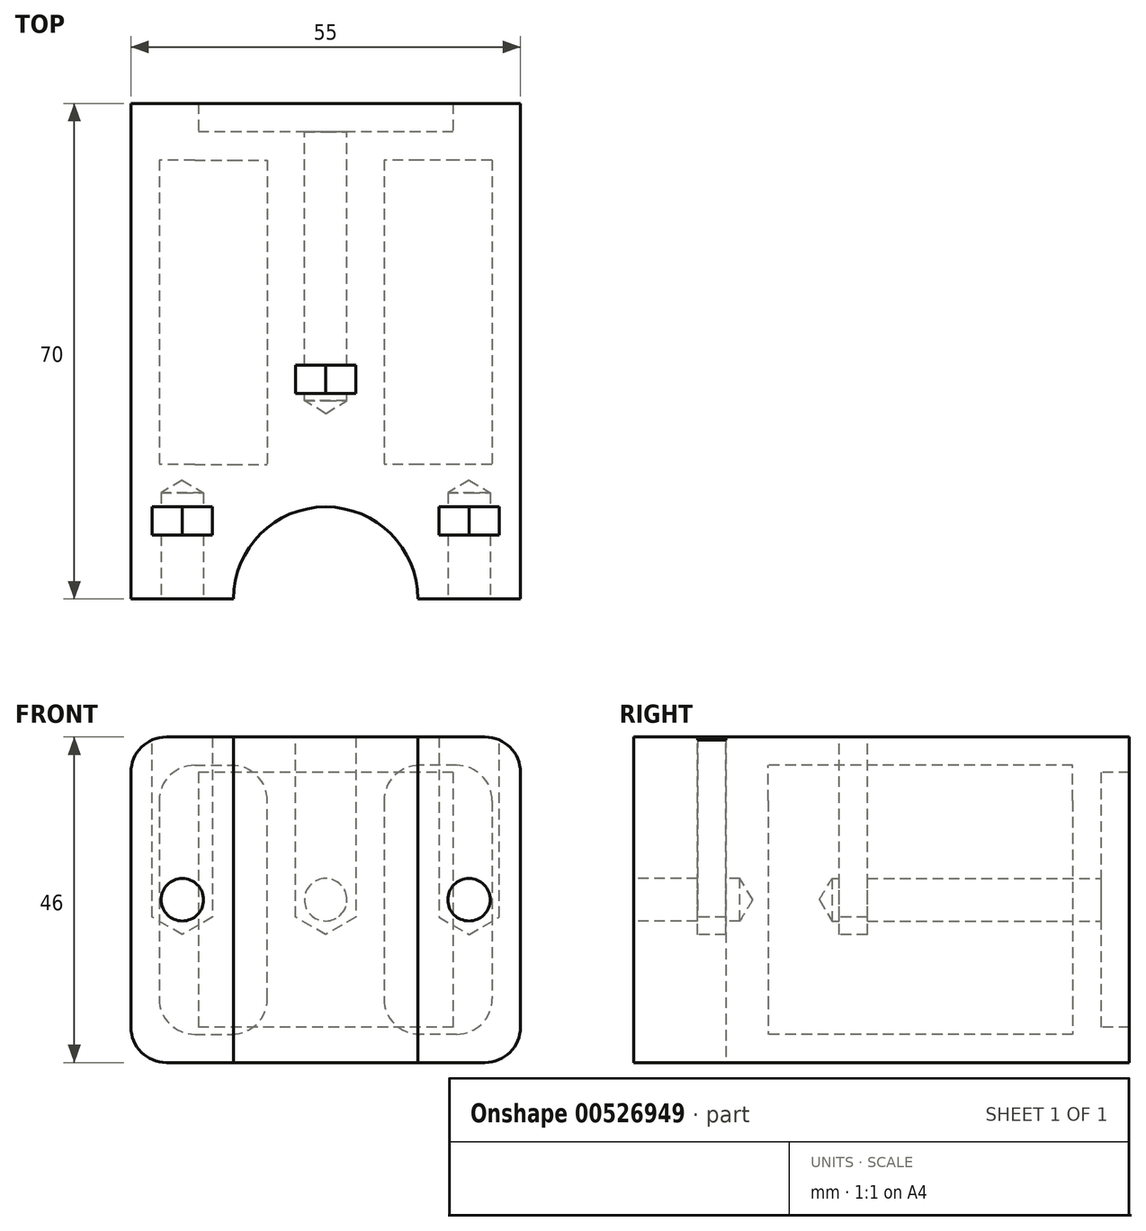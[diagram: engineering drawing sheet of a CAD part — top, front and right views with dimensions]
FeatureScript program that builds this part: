
annotation { "Feature Type Name" : "Feature", "Feature Type Description" : "" }
export const myFeature = defineFeature(function(context is Context, id is Id, definition is map)
    precondition{}
    {
        {
            var Q0;
            Q0=qCreatedBy(makeId("Front.planeOp"),FACE);
            var sketch = newSketch(context, id + "F0", { "sketchPlane" : qUnion([Q0])});
            skLineSegment(sketch, "E0.bottom", {"start": v(-27.5, 23) * mm, "end": v(27.5, 23) * mm});
            skLineSegment(sketch, "E0.top", {"start": v(-27.5, -23) * mm, "end": v(27.5, -23) * mm});
            skLineSegment(sketch, "E0.left", {"start": v(-27.5, 23) * mm, "end": v(-27.5, -23) * mm});
            skLineSegment(sketch, "E0.right", {"start": v(27.5, 23) * mm, "end": v(27.5, -23) * mm});
            skPoint(sketch, "E0.middle", {"position": v(0, 0) * mm});
            skPoint(sketch, "E1", {"position": v(-20.25, 0) * mm});
            skPoint(sketch, "E2", {"position": v(20.25, 0) * mm});
            skSolve(sketch);
        }
        {
            var Q0;
            Q0=qCreatedBy(makeId("Top.planeOp"),FACE);
            var sketch = newSketch(context, id + "F1", { "sketchPlane" : qUnion([Q0])});
            skPoint(sketch, "E3.middle", {"position": v(0, 0) * mm});
            skArc(sketch, "E4", {"start": v(-13, 0) * mm, "mid": v(0, 13) * mm, "end": v(13, 0) * mm});
            skLineSegment(sketch, "E5", {"start": v(-13, 0) * mm, "end": v(-27.5, 0) * mm});
            skLineSegment(sketch, "E6", {"start": v(-27.5, 0) * mm, "end": v(-27.5, 70) * mm});
            skLineSegment(sketch, "E7", {"start": v(-27.5, 70) * mm, "end": v(27.5, 70) * mm});
            skLineSegment(sketch, "E8", {"start": v(27.5, 70) * mm, "end": v(27.5, 0) * mm});
            skLineSegment(sketch, "E9", {"start": v(27.5, 0) * mm, "end": v(13, 0) * mm});
            skLineSegment(sketch, "E10", {"start": v(-20.25, 0) * mm, "end": v(-20.25, 70) * mm});
            skLineSegment(sketch, "E11", {"start": v(-20.25, 70) * mm, "end": v(20.25, 70) * mm});
            skLineSegment(sketch, "E12", {"start": v(20.25, 70) * mm, "end": v(20.25, 0) * mm});
            skSolve(sketch);
        }
        {
            var Q0;
            Q0=qCreatedBy(makeId("Front.planeOp"),FACE);
            cPlane(context, id + "F2", {"entities" : qUnion([Q0]), "cplaneType" : CPlaneType.OFFSET, "offset" : 9 * mm, "oppositeDirection" : true, "width" : 150 * mm, "height" : 150 * mm});
        }
        {
            var Q0;
            Q0=qCreatedBy(makeId("Front.planeOp"),FACE);
            cPlane(context, id + "F3", {"entities" : qUnion([Q0]), "cplaneType" : CPlaneType.OFFSET, "offset" : 66 * mm, "oppositeDirection" : true, "width" : 150 * mm, "height" : 150 * mm});
        }
        {
            var Q0;
            Q0=qCreatedBy(id+"F3.planeOp",FACE);
            cPlane(context, id + "F4", {"entities" : qUnion([Q0]), "cplaneType" : CPlaneType.OFFSET, "offset" : 37 * mm, "width" : 150 * mm, "height" : 150 * mm});
        }
        {
            var Q0;
            Q0=makeQuery(id+"F0.imprint","IMPRINT",FACE,{"disambiguationData":[TD([[makeQuery(id+"F0.imprint","IMPRINT",EDGE,{"derivedFrom":sQuery(id+"F0.wireOp",EDGE,"E0.bottom")}),-1.0]])]});
            extrude(context, id + "F5", {"entities" : qUnion([Q0]), "oppositeDirection" : true, "depth" : 70 * mm, "offsetDistance" : 25 * mm});
        }
        {
            var Q0;
            Q0 = qSketchRegion(id + "F1", true);
            extrude(context, id + "F6", {"entities" : qUnion([Q0]), "operationType" : NewBodyOperationType.INTERSECT, "depth" : 46 * mm, "offsetDistance" : 25 * mm, "symmetric" : true});
        }
        {
            var Q0;
            Q0=sQuery(id+"F0.wireOp",VERTEX,"E1");
            var Q1;
            Q1=sQuery(id+"F0.wireOp",VERTEX,"E2");
            var Q2;
            Q2=makeQuery(id+"F5.opExtrude","SWEPT_BODY",BODY,{"disambiguationData":[OSD([sQuery(id+"F0.wireOp",EDGE,"E0.bottom"),sQuery(id+"F0.wireOp",EDGE,"E0.top"),sQuery(id+"F0.wireOp",EDGE,"E0.left"),sQuery(id+"F0.wireOp",EDGE,"E0.right")])]});
            hole(context, id + "F7", {"style" : HoleStyle.SIMPLE, "endStyle" : HoleEndStyle.BLIND, "holeDiameter" : 6 * mm, "holeDepth" : 15 * mm, "isTappedThrough" : true, "tappedDepth" : 12 * mm, "tapClearance" : 3, "locations" : qUnion([Q0, Q1]), "scope" : qUnion([Q2])});
        }
        {
            var Q0;
            Q0=qCreatedBy(id+"F2.planeOp",FACE);
            var sketch = newSketch(context, id + "F8", { "sketchPlane" : qUnion([Q0])});
            skPoint(sketch, "E13", {"position": v(-20.25, 0) * mm});
            skPoint(sketch, "E14", {"position": v(20.25, 0) * mm});
            skLineSegment(sketch, "E15", {"start": v(-24.5, 2.25) * mm, "end": v(-24.5, 23) * mm});
            skLineSegment(sketch, "E16", {"start": v(-24.5, 23) * mm, "end": v(-16, 23) * mm});
            skLineSegment(sketch, "E17", {"start": v(-16, 23) * mm, "end": v(-16, 2) * mm});
            skCircle(sketch, "E18.cCircle", {"center": v(-20.25, 0) * mm, "radius": 4.9 * mm, "construction": true});
            skLineSegment(sketch, "E18.0", {"start": v(-20.25, 4.9) * mm, "end": v(-16, 2.45) * mm});
            skLineSegment(sketch, "E18.1", {"start": v(-16, 2.45) * mm, "end": v(-16, -2.45) * mm});
            skLineSegment(sketch, "E18.2", {"start": v(-16, -2.45) * mm, "end": v(-20.25, -4.9) * mm});
            skLineSegment(sketch, "E18.3", {"start": v(-20.25, -4.9) * mm, "end": v(-24.5, -2.45) * mm});
            skLineSegment(sketch, "E18.4", {"start": v(-24.5, -2.45) * mm, "end": v(-24.5, 2.45) * mm});
            skLineSegment(sketch, "E18.5", {"start": v(-24.5, 2.45) * mm, "end": v(-20.25, 4.9) * mm});
            skLineSegment(sketch, "E19.MirrorCS", {"start": v(24.5, 23) * mm, "end": v(16, 23) * mm});
            skLineSegment(sketch, "E20.MirrorCS", {"start": v(24.5, 2.25) * mm, "end": v(24.5, 23) * mm});
            skLineSegment(sketch, "E21.MirrorCS", {"start": v(16, 23) * mm, "end": v(16, 2) * mm});
            skLineSegment(sketch, "E22.MirrorCS", {"start": v(24.5, -2.45) * mm, "end": v(24.5, 2.45) * mm});
            skLineSegment(sketch, "E23.MirrorCS", {"start": v(16, 2.45) * mm, "end": v(16, -2.45) * mm});
            skLineSegment(sketch, "E24.MirrorCS", {"start": v(16, -2.45) * mm, "end": v(20.25, -4.9) * mm});
            skLineSegment(sketch, "E25.MirrorCS", {"start": v(20.25, -4.9) * mm, "end": v(24.5, -2.45) * mm});
            skSolve(sketch);
        }
        {
            var Q0;
            Q0 = qSketchRegion(id + "F8", true);
            extrude(context, id + "F9", {"entities" : qUnion([Q0]), "operationType" : NewBodyOperationType.REMOVE, "oppositeDirection" : true, "depth" : 4 * mm, "offsetDistance" : 25 * mm});
        }
        {
            var Q0;
            Q0=qCreatedBy(id+"F3.planeOp",FACE);
            var sketch = newSketch(context, id + "F10", { "sketchPlane" : qUnion([Q0])});
            skPoint(sketch, "E26", {"position": v(0, 0) * mm});
            skLineSegment(sketch, "E27.bottom", {"start": v(18, 18) * mm, "end": v(-18, 18) * mm});
            skLineSegment(sketch, "E27.top", {"start": v(18, -18) * mm, "end": v(-18, -18) * mm});
            skLineSegment(sketch, "E27.left", {"start": v(18, 18) * mm, "end": v(18, -18) * mm});
            skLineSegment(sketch, "E27.right", {"start": v(-18, 18) * mm, "end": v(-18, -18) * mm});
            skSolve(sketch);
        }
        {
            var Q0;
            Q0 = qSketchRegion(id + "F10", true);
            extrude(context, id + "F11", {"entities" : qUnion([Q0]), "operationType" : NewBodyOperationType.REMOVE, "oppositeDirection" : true, "depth" : 4 * mm, "offsetDistance" : 25 * mm});
        }
        {
            var Q0;
            Q0=sQuery(id+"F10.wireOp",VERTEX,"E26");
            var Q1;
            Q1=makeQuery(id+"F5.opExtrude","SWEPT_BODY",BODY,{"disambiguationData":[OSD([sQuery(id+"F0.wireOp",EDGE,"E0.bottom"),sQuery(id+"F0.wireOp",EDGE,"E0.top"),sQuery(id+"F0.wireOp",EDGE,"E0.left"),sQuery(id+"F0.wireOp",EDGE,"E0.right")])]});
            hole(context, id + "F12", {"style" : HoleStyle.SIMPLE, "endStyle" : HoleEndStyle.BLIND, "oppositeDirection" : true, "holeDiameter" : 6 * mm, "holeDepth" : 38 * mm, "isTappedThrough" : true, "tappedDepth" : 12 * mm, "tapClearance" : 3, "locations" : qUnion([Q0]), "scope" : qUnion([Q1])});
        }
        {
            var Q0;
            Q0=qCreatedBy(id+"F4.planeOp",FACE);
            var sketch = newSketch(context, id + "F13", { "sketchPlane" : qUnion([Q0])});
            skLineSegment(sketch, "E28", {"start": v(-4.25, 2.25) * mm, "end": v(-4.25, 23) * mm});
            skLineSegment(sketch, "E29", {"start": v(-4.25, 23) * mm, "end": v(4.25, 23) * mm});
            skLineSegment(sketch, "E30", {"start": v(4.25, 23) * mm, "end": v(4.25, 2.07) * mm});
            skPoint(sketch, "E31", {"position": v(0, 0) * mm});
            skCircle(sketch, "E32.cCircle", {"center": v(0, 0) * mm, "radius": 4.9 * mm, "construction": true});
            skLineSegment(sketch, "E32.0", {"start": v(4.25, 2.45) * mm, "end": v(4.25, -2.45) * mm});
            skLineSegment(sketch, "E32.1", {"start": v(4.25, -2.45) * mm, "end": v(0, -4.9) * mm});
            skLineSegment(sketch, "E32.2", {"start": v(0, -4.9) * mm, "end": v(-4.25, -2.45) * mm});
            skLineSegment(sketch, "E32.3", {"start": v(-4.25, -2.45) * mm, "end": v(-4.25, 2.45) * mm});
            skLineSegment(sketch, "E32.4", {"start": v(-4.25, 2.45) * mm, "end": v(0, 4.9) * mm});
            skLineSegment(sketch, "E32.5", {"start": v(0, 4.9) * mm, "end": v(4.25, 2.45) * mm});
            skLineSegment(sketch, "E33.bottom", {"start": v(18.5, 19) * mm, "end": v(13.25, 19) * mm});
            skLineSegment(sketch, "E33.top", {"start": v(18.5, -19) * mm, "end": v(13.25, -19) * mm});
            skLineSegment(sketch, "E33.left", {"start": v(23.5, 14) * mm, "end": v(23.5, -14) * mm});
            skLineSegment(sketch, "E34.MirrorCS", {"start": v(-18.5, 19) * mm, "end": v(-13.25, 19) * mm});
            skLineSegment(sketch, "E35.MirrorCS", {"start": v(-23.5, 14) * mm, "end": v(-23.5, -14) * mm});
            skLineSegment(sketch, "E36.MirrorCS", {"start": v(-18.5, -19) * mm, "end": v(-13.25, -19) * mm});
            skLineSegment(sketch, "E37", {"start": v(8.25, 14) * mm, "end": v(8.25, -14) * mm});
            skLineSegment(sketch, "E38", {"start": v(-8.25, -14) * mm, "end": v(-8.25, 14) * mm});
            skPoint(sketch, "E39.visualSharp", {"position": v(23.5, 19) * mm});
            skArc(sketch, "E39.filletArc", {"start": v(23.5, 14) * mm, "mid": v(22.04, 17.54) * mm, "end": v(18.5, 19) * mm});
            skPoint(sketch, "E40.visualSharp", {"position": v(8.25, 19) * mm});
            skArc(sketch, "E40.filletArc", {"start": v(13.25, 19) * mm, "mid": v(9.71, 17.54) * mm, "end": v(8.25, 14) * mm});
            skPoint(sketch, "E41.visualSharp", {"position": v(-8.25, 19) * mm});
            skArc(sketch, "E41.filletArc", {"start": v(-8.25, 14) * mm, "mid": v(-9.71, 17.54) * mm, "end": v(-13.25, 19) * mm});
            skPoint(sketch, "E42.visualSharp", {"position": v(-23.5, 19) * mm});
            skArc(sketch, "E42.filletArc", {"start": v(-18.5, 19) * mm, "mid": v(-22.04, 17.54) * mm, "end": v(-23.5, 14) * mm});
            skPoint(sketch, "E43.visualSharp", {"position": v(23.5, -19) * mm});
            skArc(sketch, "E43.filletArc", {"start": v(18.5, -19) * mm, "mid": v(22.04, -17.54) * mm, "end": v(23.5, -14) * mm});
            skPoint(sketch, "E44.visualSharp", {"position": v(-23.5, -19) * mm});
            skArc(sketch, "E44.filletArc", {"start": v(-23.5, -14) * mm, "mid": v(-22.04, -17.54) * mm, "end": v(-18.5, -19) * mm});
            skPoint(sketch, "E45.newPointA", {"position": v(8.25, -18.96) * mm});
            skPoint(sketch, "E45.newPointB", {"position": v(8.25, -19) * mm});
            skArc(sketch, "E45.filletArc", {"start": v(8.25, -14) * mm, "mid": v(9.71, -17.54) * mm, "end": v(13.25, -19) * mm});
            skPoint(sketch, "E46.newPointA", {"position": v(-8.25, -18.96) * mm});
            skPoint(sketch, "E46.newPointB", {"position": v(-8.25, -19) * mm});
            skArc(sketch, "E46.filletArc", {"start": v(-13.25, -19) * mm, "mid": v(-9.71, -17.54) * mm, "end": v(-8.25, -14) * mm});
            skSolve(sketch);
        }
        {
            var Q0;
            Q0 = qSketchRegion(id + "F13", true);
            extrude(context, id + "F14", {"entities" : qUnion([Q0]), "operationType" : NewBodyOperationType.REMOVE, "oppositeDirection" : true, "depth" : 4 * mm, "offsetDistance" : 25 * mm});
        }
        {
            var Q0;
            Q0=makeQuery(id+"F5.opExtrude","SWEPT_EDGE",EDGE,{"disambiguationData":[OSD([sQuery(id+"F0.wireOp",EDGE,"E0.bottom"),sQuery(id+"F0.wireOp",EDGE,"E0.left")])]});
            var Q1;
            Q1=makeQuery(id+"F5.opExtrude","SWEPT_EDGE",EDGE,{"disambiguationData":[OSD([sQuery(id+"F0.wireOp",EDGE,"E0.bottom"),sQuery(id+"F0.wireOp",EDGE,"E0.right")])]});
            var Q2;
            Q2=makeQuery(id+"F5.opExtrude","SWEPT_EDGE",EDGE,{"disambiguationData":[OSD([sQuery(id+"F0.wireOp",EDGE,"E0.top"),sQuery(id+"F0.wireOp",EDGE,"E0.left")])]});
            var Q3;
            Q3=makeQuery(id+"F5.opExtrude","SWEPT_EDGE",EDGE,{"disambiguationData":[OSD([sQuery(id+"F0.wireOp",EDGE,"E0.top"),sQuery(id+"F0.wireOp",EDGE,"E0.right")])]});
            fillet(context, id + "F15", {"entities" : qUnion([Q0, Q1, Q2, Q3]), "radius" : 5 * mm, "tangentPropagation" : true, "allowEdgeOverflow" : false});
        }
        {
            var Q0;
            Q0=makeQuery(id+"F13.imprint","IMPRINT",FACE,{"disambiguationData":[TD([[makeQuery(id+"F13.imprint","IMPRINT",EDGE,{"derivedFrom":sQuery(id+"F13.wireOp",EDGE,"E33.bottom")}),1.0]])]});
            var Q1;
            Q1=makeQuery(id+"F13.imprint","IMPRINT",FACE,{"disambiguationData":[TD([[makeQuery(id+"F13.imprint","IMPRINT",EDGE,{"derivedFrom":sQuery(id+"F13.wireOp",EDGE,"E34.MirrorCS")}),-1.0]])]});
            extrude(context, id + "F16", {"entities" : qUnion([Q0, Q1]), "operationType" : NewBodyOperationType.REMOVE, "oppositeDirection" : true, "depth" : 33 * mm, "offsetDistance" : 25 * mm});
        }
        {
            var Q0;
            Q0=makeQuery(id+"F13.imprint","IMPRINT",FACE,{"disambiguationData":[TD([[makeQuery(id+"F13.imprint","IMPRINT",EDGE,{"derivedFrom":sQuery(id+"F13.wireOp",EDGE,"E33.bottom")}),1.0]])]});
            var Q1;
            Q1=makeQuery(id+"F13.imprint","IMPRINT",FACE,{"disambiguationData":[TD([[makeQuery(id+"F13.imprint","IMPRINT",EDGE,{"derivedFrom":sQuery(id+"F13.wireOp",EDGE,"E34.MirrorCS")}),-1.0]])]});
            extrude(context, id + "F17", {"entities" : qUnion([Q0, Q1]), "operationType" : NewBodyOperationType.REMOVE, "depth" : 10 * mm, "offsetDistance" : 25 * mm});
        }
    });
